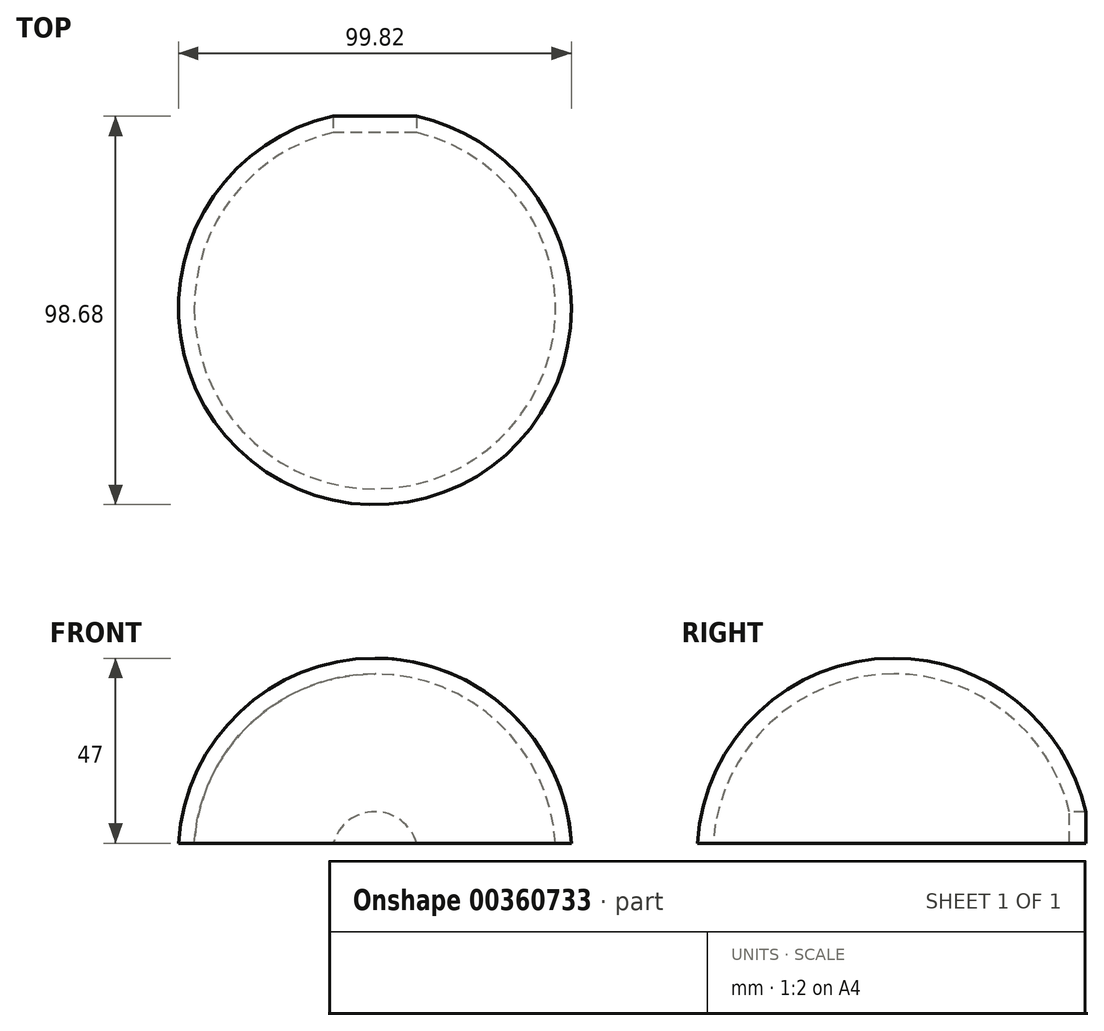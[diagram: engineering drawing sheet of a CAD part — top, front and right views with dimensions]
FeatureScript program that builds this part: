
annotation { "Feature Type Name" : "Feature", "Feature Type Description" : "" }
export const myFeature = defineFeature(function(context is Context, id is Id, definition is map)
    precondition{}
    {
        {
            var Q0;
            Q0=qCreatedBy(makeId("Front.planeOp"),FACE);
            var sketch = newSketch(context, id + "F0", { "sketchPlane" : qUnion([Q0])});
            skArc(sketch, "E0", {"start": v(0, 50) * mm, "mid": v(-34.28, 36.4) * mm, "end": v(-49.9, 3) * mm});
            skArc(sketch, "E1", {"start": v(0, 46) * mm, "mid": v(-31.45, 33.57) * mm, "end": v(-45.9, 3) * mm});
            skLineSegment(sketch, "E2", {"start": v(-49.9, 3) * mm, "end": v(-45.9, 3) * mm});
            skLineSegment(sketch, "E3", {"start": v(0, 46) * mm, "end": v(0, 50) * mm});
            skLineSegment(sketch, "E4", {"start": v(0, 50) * mm, "end": v(0, 0) * mm});
            skSolve(sketch);
        }
        {
            var Q0;
            {var subQ0=sQuery(id+"F0.wireOp",EDGE,"E0");Q0=makeQuery(id+"F0.imprint","IMPRINT",FACE,{"disambiguationData":[TD([[makeQuery(id+"F0.imprint","IMPRINT",EDGE,{"derivedFrom":subQ0}),1.0]])]});}
            var Q1;
            Q1=sQuery(id+"F0.wireOp",EDGE,"E4");
            revolve(context, id + "F1", {"entities" : qUnion([Q0]), "axis" : qUnion([Q1]), "revolveType" : RevolveType.FULL});
        }
        {
            var Q0;
            Q0=qCreatedBy(makeId("Front.planeOp"),FACE);
            var sketch = newSketch(context, id + "F2", { "sketchPlane" : qUnion([Q0])});
            skCircle(sketch, "E5", {"center": v(0, 0) * mm, "radius": 11 * mm});
            skSolve(sketch);
        }
        {
            var Q0;
            Q0=sQuery(id+"F2.wireOp",VERTEX,"E5.center");
            var Q1;
            Q1=makeQuery(id+"F1.opRevolve","SWEPT_BODY",BODY,{"disambiguationData":[OSD([sQuery(id+"F0.wireOp",EDGE,"E0"),sQuery(id+"F0.wireOp",EDGE,"E1"),sQuery(id+"F0.wireOp",EDGE,"E2"),sQuery(id+"F0.wireOp",EDGE,"E4")])]});
            hole(context, id + "F3", {"style" : HoleStyle.SIMPLE, "endStyle" : HoleEndStyle.THROUGH, "holeDiameter" : 22 * mm, "isTappedThrough" : true, "tappedDepth" : 12.7 * mm, "tapClearance" : 3, "locations" : qUnion([Q0]), "scope" : qUnion([Q1])});
        }
    });
